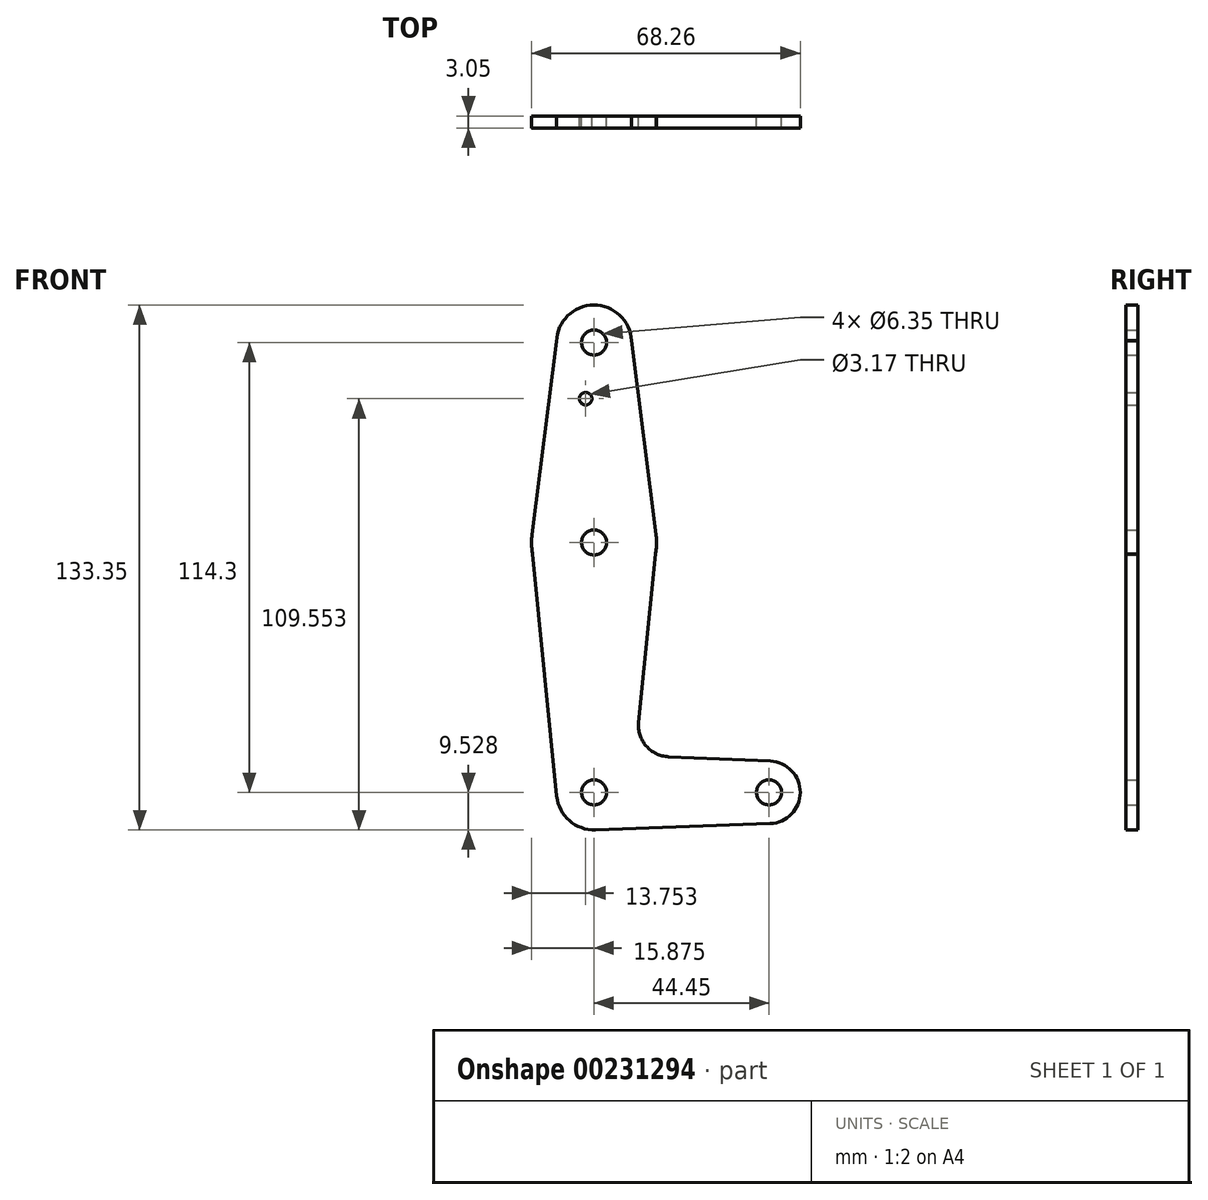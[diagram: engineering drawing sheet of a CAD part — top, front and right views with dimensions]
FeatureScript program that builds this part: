
annotation { "Feature Type Name" : "Feature", "Feature Type Description" : "" }
export const myFeature = defineFeature(function(context is Context, id is Id, definition is map)
    precondition{}
    {
        {
            var Q0;
            Q0=qCreatedBy(makeId("Front.planeOp"),FACE);
            var sketch = newSketch(context, id + "F0", { "sketchPlane" : qUnion([Q0])});
            skLineSegment(sketch, "E0", {"start": v(-54.3, 83.09) * mm, "end": v(-54.3, -31.21) * mm, "construction": true});
            skLineSegment(sketch, "E1", {"start": v(-54.3, -31.21) * mm, "end": v(-9.84, -31.21) * mm, "construction": true});
            skCircle(sketch, "E2", {"center": v(-54.3, 83.09) * mm, "radius": 9.53 * mm});
            skCircle(sketch, "E3", {"center": v(-54.3, 32.29) * mm, "radius": 15.88 * mm});
            skCircle(sketch, "E4", {"center": v(-54.3, -31.21) * mm, "radius": 9.53 * mm});
            skCircle(sketch, "E5", {"center": v(-9.84, -31.21) * mm, "radius": 7.94 * mm});
            skLineSegment(sketch, "E6", {"start": v(-63.82, 83.35) * mm, "end": v(-70.04, 34.29) * mm});
            skLineSegment(sketch, "E7", {"start": v(-44.78, 83.55) * mm, "end": v(-38.55, 34.28) * mm});
            skLineSegment(sketch, "E8", {"start": v(-70.17, 32.11) * mm, "end": v(-63.77, -32.16) * mm});
            skLineSegment(sketch, "E9", {"start": v(-38.42, 32.12) * mm, "end": v(-42.95, -13.43) * mm});
            skLineSegment(sketch, "E10", {"start": v(-35.39, -22.16) * mm, "end": v(-9.5, -23.28) * mm});
            skLineSegment(sketch, "E11", {"start": v(-53.97, -40.73) * mm, "end": v(-9.56, -39.14) * mm});
            skCircle(sketch, "E12", {"center": v(-54.3, 83.09) * mm, "radius": 3.18 * mm});
            skCircle(sketch, "E13", {"center": v(-54.3, 32.29) * mm, "radius": 3.18 * mm});
            skCircle(sketch, "E14", {"center": v(-54.3, -31.21) * mm, "radius": 3.18 * mm});
            skCircle(sketch, "E15", {"center": v(-9.84, -31.21) * mm, "radius": 3.18 * mm});
            skArc(sketch, "E16.filletArc", {"start": v(-42.95, -13.43) * mm, "mid": v(-41.05, -19.43) * mm, "end": v(-35.39, -22.16) * mm});
            skCircle(sketch, "E17", {"center": v(-56.42, 68.81) * mm, "radius": 1.59 * mm});
            skSolve(sketch);
        }
        {
            var Q0;
            Q0 = qSketchRegion(id + "F0", true);
            extrude(context, id + "F1", {"entities" : qUnion([Q0]), "depth" : 3.05 * mm});
        }
    });
